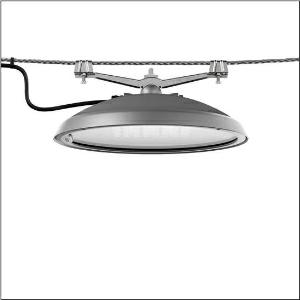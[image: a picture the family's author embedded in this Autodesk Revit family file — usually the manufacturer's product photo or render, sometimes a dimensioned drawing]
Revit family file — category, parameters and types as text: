
# Revit family: dl_r__50_iq_mini___st1_0s_5xa248w31f08he_c7f4
name_source: partatom
category: Lighting Fixtures
units: mm (PartAtom-declared; Revit-internal decimal feet)

## family parameters
Cut with Voids When Loaded = No
Host = Face
Light Source = No
Part Type = Normal
Room Calculation Point = No
Round Connector Dimension = Use Diameter
Shared = No

## types (1)
- --- (1 x LED, 9400 lm, 68.6 W, 3000K)
    Apparent Load = 69 VA
    CIE Flux Codes = 37 72 97 100 100
    Color Rendering = 70
    Color Temperature = 3000K
    Default Elevation = 1800 mm
    Description = DL® 50 iQ mini, catenary luminaire, primary light control with lens, of PMMA, primary optical cover: cover, of toughened safety glass, transparent, light distribution: ST1.0s, light emission: direct distribution, primary light characteristic: symmetric, installation type: suspended mounting, LED, High Power LED, rated luminous flux: 9.400lm, luminous efficacy: 137lm/W, light colour: 730, colour temperature: 3000K, control: optimised constant luminous flux control (CLO 2.0), Desk-Remote (wireless, voltage-free reading and setting of iQ features in the workshop via application-optimized NFC function/RFID function), Light-Fading, Smart-Wire, Night-Set, Lumen-Switch, Temp-Guard, Auto-Match, Street-Remote, mains connection: 230..240V, AC, 50/60Hz, start of lifetime: 69W, end of service life: 72W, reduction: 30W, luminaire housing, of diecast aluminium, powder-coated, Siteco® metallic grey (DB 702S), diameter: 500mm, height: 115mm, protection rating (complete): IP66, insulation class (complete): insulation class II (safety insulation), certification: CE, ENEC, VDE, impact resistance: IK08, permissible operating ambient temperature for outdoor applications: -25..+40°C, standard-compliant lighting for roads and squares, packaging unit: 1 piece

Light Distribution: ST1.0s
    Height = 124 mm
    Lamp = 1 x LED
    Lamp Light Flux = 9400 lm
    Lamp Power = 68.6 W
    Lamp count = 1
    Length = 500 mm
    Luminous efficacy = 137 lm/W
    Manufacturer = Siteco
    ModVariant = No
    Model = 5XA248W31F08HE
    Number of Poles = 1
    OnlyDefault = Yes
    Power Factor = 1
    Product Name = DL® 50 iQ mini | ST1.0s
    Product group = catenary luminaire
    ProductGroupID = 6300
    Protection Class = Protection class II
    Protection Degree = IP 66
    RLX_Detail_Level = 1
    RLX_Emergency_Light_Flux = 0 lm
    RLX_Emergency_Type = 0
    RLX_Emergency_Type_DB = No
    RlxData = <blob elided: 123845 chars, md5=2f017e66>
    Socket = socket
    Standby Power = 0 W
    System Light Flux = 9400 lm
    System Power = 69 W
    Type Comments = factory setting: luminous flux: 100 % | dim-lin: 254 | 693 mA
    Type Image = l_1242791.jpg
    URL = http://relux.com
    VarID = @adj_071965
    Voltage = 0 V
    Weight = 0.00 kg
    Width = 0 mm  [stored 0 ft]

note: [stored X ft] marks values corroborated as IEEE doubles in the binary element streams (Revit-internal decimal feet)

## geometry (parser evidence)
native form markers: Blend x4, Sweep x11
no freeform markers — native parametric forms only
